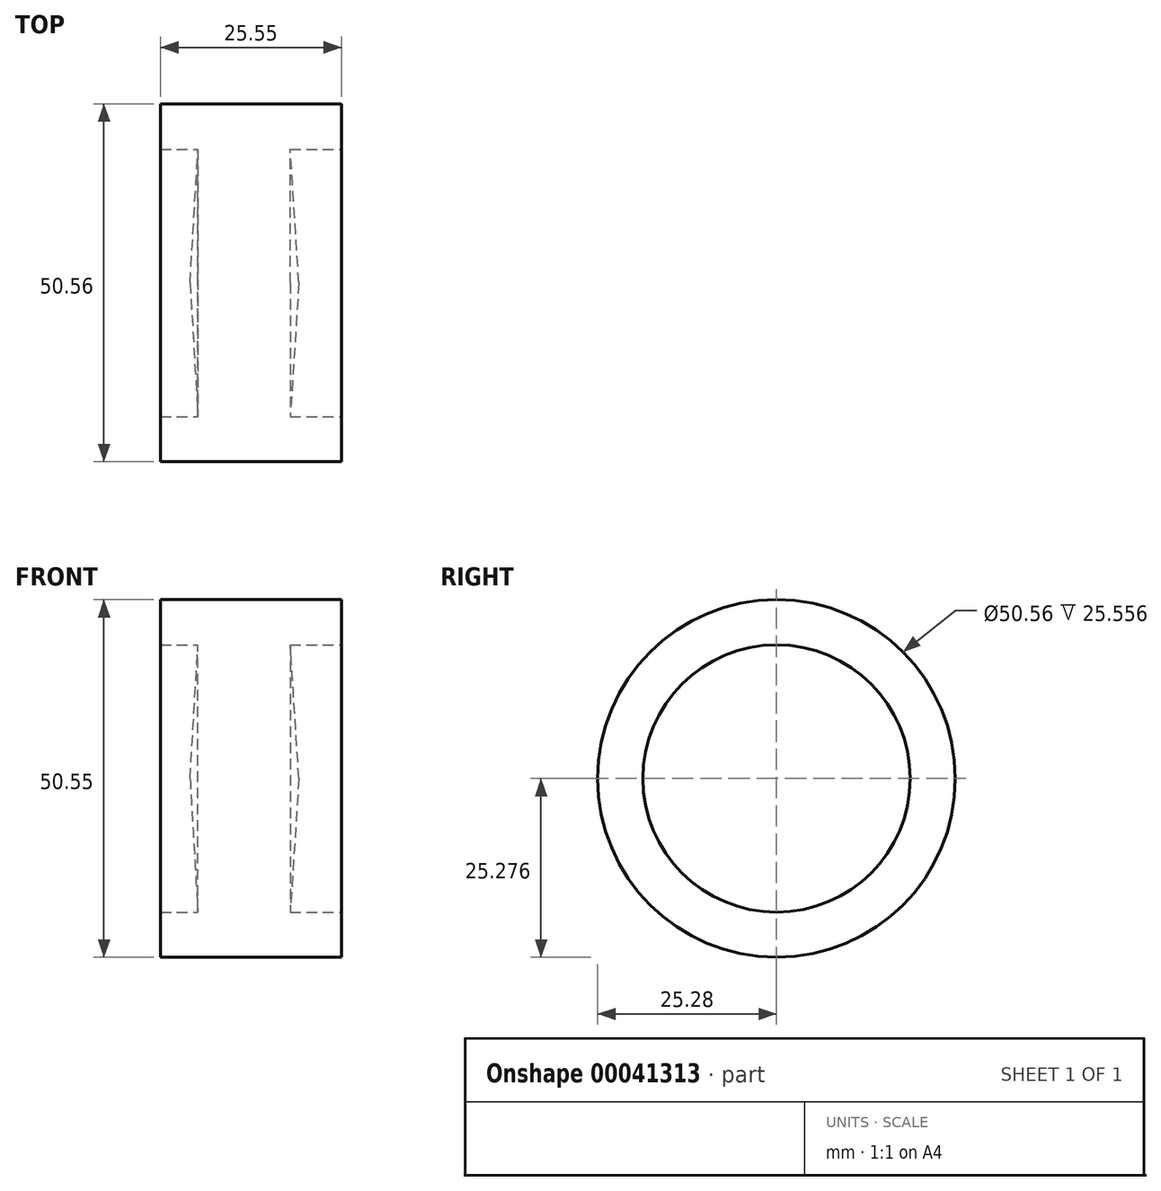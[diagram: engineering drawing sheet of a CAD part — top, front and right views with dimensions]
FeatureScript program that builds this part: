
annotation { "Feature Type Name" : "Feature", "Feature Type Description" : "" }
export const myFeature = defineFeature(function(context is Context, id is Id, definition is map)
    precondition{}
    {
        {
            var Q0;
            Q0=qCreatedBy(makeId("Front.planeOp"),FACE);
            var sketch = newSketch(context, id + "F0", { "sketchPlane" : qUnion([Q0])});
            skLineSegment(sketch, "E0", {"start": v(-62.08, 52.08) * mm, "end": v(-36.53, 52.08) * mm});
            skLineSegment(sketch, "E1", {"start": v(-36.53, 52.08) * mm, "end": v(-36.53, 45.7) * mm});
            skLineSegment(sketch, "E2", {"start": v(-36.53, 45.7) * mm, "end": v(-43.75, 45.7) * mm});
            skLineSegment(sketch, "E3", {"start": v(-43.75, 45.7) * mm, "end": v(-42.54, 26.8) * mm});
            skLineSegment(sketch, "E4", {"start": v(-57.91, 26.8) * mm, "end": v(-56.8, 45.7) * mm});
            skLineSegment(sketch, "E5", {"start": v(-56.8, 45.7) * mm, "end": v(-62.08, 45.7) * mm});
            skLineSegment(sketch, "E6", {"start": v(-62.08, 45.7) * mm, "end": v(-62.08, 52.08) * mm});
            skLineSegment(sketch, "E7", {"start": v(-70.42, 26.8) * mm, "end": v(-21.8, 26.8) * mm, "construction": true});
            skSolve(sketch);
        }
        {
            var Q0;
            Q0 = qSketchRegion(id + "F0", true);
            var Q1;
            Q1 = qConstructionFilter(qBodyType(qCreatedBy(id + "F0" ,EDGE), BodyType.WIRE), ConstructionObject.NO);
            var Q2;
            Q2=sQuery(id+"F0.wireOp",EDGE,"E7");
            revolve(context, id + "F1", {"bodyType" : ToolBodyType.SURFACE, "entities" : qUnion([Q0]), "surfaceEntities" : qUnion([Q1]), "axis" : qUnion([Q2]), "revolveType" : RevolveType.FULL});
        }
    });
